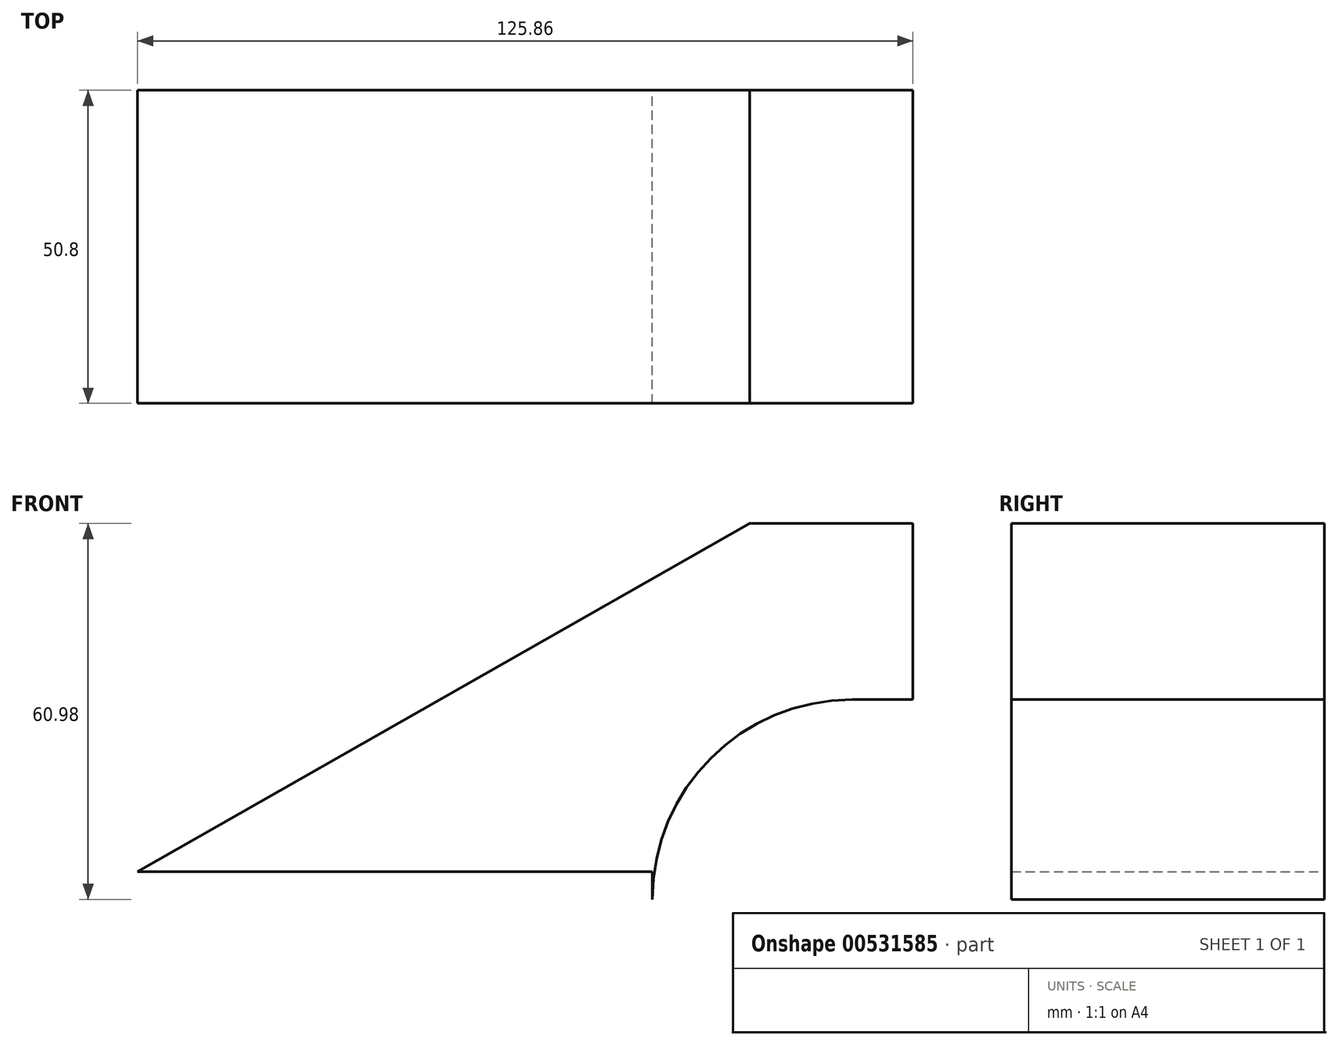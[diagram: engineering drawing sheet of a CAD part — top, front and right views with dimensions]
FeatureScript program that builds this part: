
annotation { "Feature Type Name" : "Feature", "Feature Type Description" : "" }
export const myFeature = defineFeature(function(context is Context, id is Id, definition is map)
    precondition{}
    {
        {
            var Q0;
            Q0=qCreatedBy(makeId("Front.planeOp"),FACE);
            var sketch = newSketch(context, id + "F0", { "sketchPlane" : qUnion([Q0])});
            skLineSegment(sketch, "E0.bottom", {"start": v(-41.78, -9.53) * mm, "end": v(41.78, -9.53) * mm});
            skLineSegment(sketch, "E0.top", {"start": v(-41.78, 9.53) * mm, "end": v(41.78, 9.53) * mm});
            skLineSegment(sketch, "E0.left", {"start": v(-41.78, -9.53) * mm, "end": v(-41.78, 9.53) * mm});
            skLineSegment(sketch, "E0.right", {"start": v(41.78, -9.53) * mm, "end": v(41.78, 9.52) * mm});
            skPoint(sketch, "E0.middle", {"position": v(0, 0) * mm});
            skLineSegment(sketch, "E1", {"start": v(41.78, 5.03) * mm, "end": v(41.78, 9.52) * mm});
            skArc(sketch, "E2", {"start": v(41.78, 5.03) * mm, "mid": v(51.28, 27.94) * mm, "end": v(74.2, 37.44) * mm});
            skLineSegment(sketch, "E3", {"start": v(71.57, 37.44) * mm, "end": v(74.2, 37.44) * mm});
            skLineSegment(sketch, "E4.bottom", {"start": v(84.08, 37.44) * mm, "end": v(57.58, 37.44) * mm});
            skLineSegment(sketch, "E4.top", {"start": v(84.08, 66.01) * mm, "end": v(57.58, 66.01) * mm});
            skLineSegment(sketch, "E4.left", {"start": v(84.08, 37.44) * mm, "end": v(84.08, 66.01) * mm});
            skLineSegment(sketch, "E4.right", {"start": v(57.58, 37.44) * mm, "end": v(57.58, 66.01) * mm});
            skPoint(sketch, "E4.middle", {"position": v(70.83, 51.72) * mm});
            skArc(sketch, "E5.0", {"start": v(60.83, 5.03) * mm, "mid": v(64.75, 14.47) * mm, "end": v(74.2, 18.39) * mm});
            skFitSpline(sketch, "E6", {"points": [v(-41.78, 9.52) * mm, v(57.58, 66.01) * mm], "startDerivative": vector(99.36, 56.49) * mm, "endDerivative": vector(99.36, 56.49) * mm});
            skSolve(sketch);
        }
        {
            var Q0;
            Q0=makeQuery(id+"F0.imprint","IMPRINT",FACE,{"disambiguationData":[TD([[makeQuery(id+"F0.imprint","IMPRINT",EDGE,{"derivedFrom":sQuery(id+"F0.wireOp",EDGE,"E0.top")}),1.0]])]});
            var Q1;
            Q1=makeQuery(id+"F0.imprint","IMPRINT",FACE,{"disambiguationData":[TD([[makeQuery(id+"F0.imprint","IMPRINT",EDGE,{"derivedFrom":sQuery(id+"F0.wireOp",EDGE,"E4.top")}),1.0]])]});
            extrude(context, id + "F1", {"entities" : qUnion([Q0, Q1]), "endBound" : BoundingType.SYMMETRIC, "depth" : 50.8 * mm, "offsetDistance" : 25.4 * mm});
        }
    });
